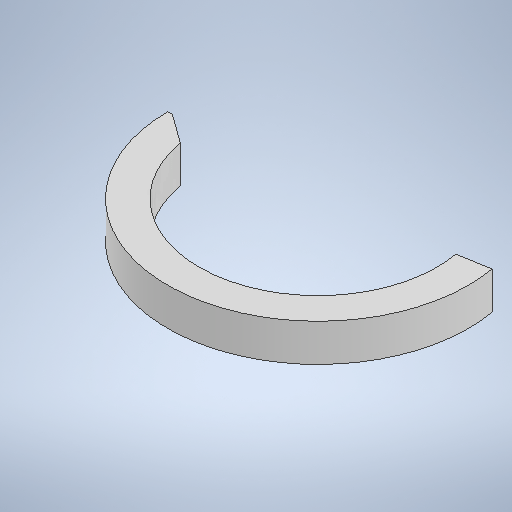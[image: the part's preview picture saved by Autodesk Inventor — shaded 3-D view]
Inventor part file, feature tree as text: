
AUTODESK INVENTOR PART (.ipt)
format: ipt  version: 2025 (Build 290162000, 162)  size: 272,896 bytes
history: native  units: in
note: dims shown in document units (in); Inventor stores cm internally (conversion verified against a paired STEP export)
features: sketch x2, revolve x1, extrude x1
ambient origin geometry x8: Origin, YZ Plane, XZ Plane, XY Plane, X Axis, Y Axis, Z Axis, Center Point
bodies: Solid1 (feature_tree)
feature tree (4):
  revolve  "Revolution1"  [1 undecoded]
  extrude  "Extrusion1"  Depth=0.0787in
  sketch  "Sketch1"  dims[d0=0.8661in d2=0.5906in]
  sketch  "Sketch2"  dims[d3=0.1181in d4=0.9843in d5=0.8268in d6=0.2953in d7=0.0in d8=3.5433in d9=0.0787in d10=1.3056in d12=0.0687in d13=0.3937in d14=0.0in d15=0.0in]
note: 1 required parameter value undecoded (feature->parameter linkage not recoverable at this tier; creation-order binding heuristic only, values carry confidence <= 0.55)
